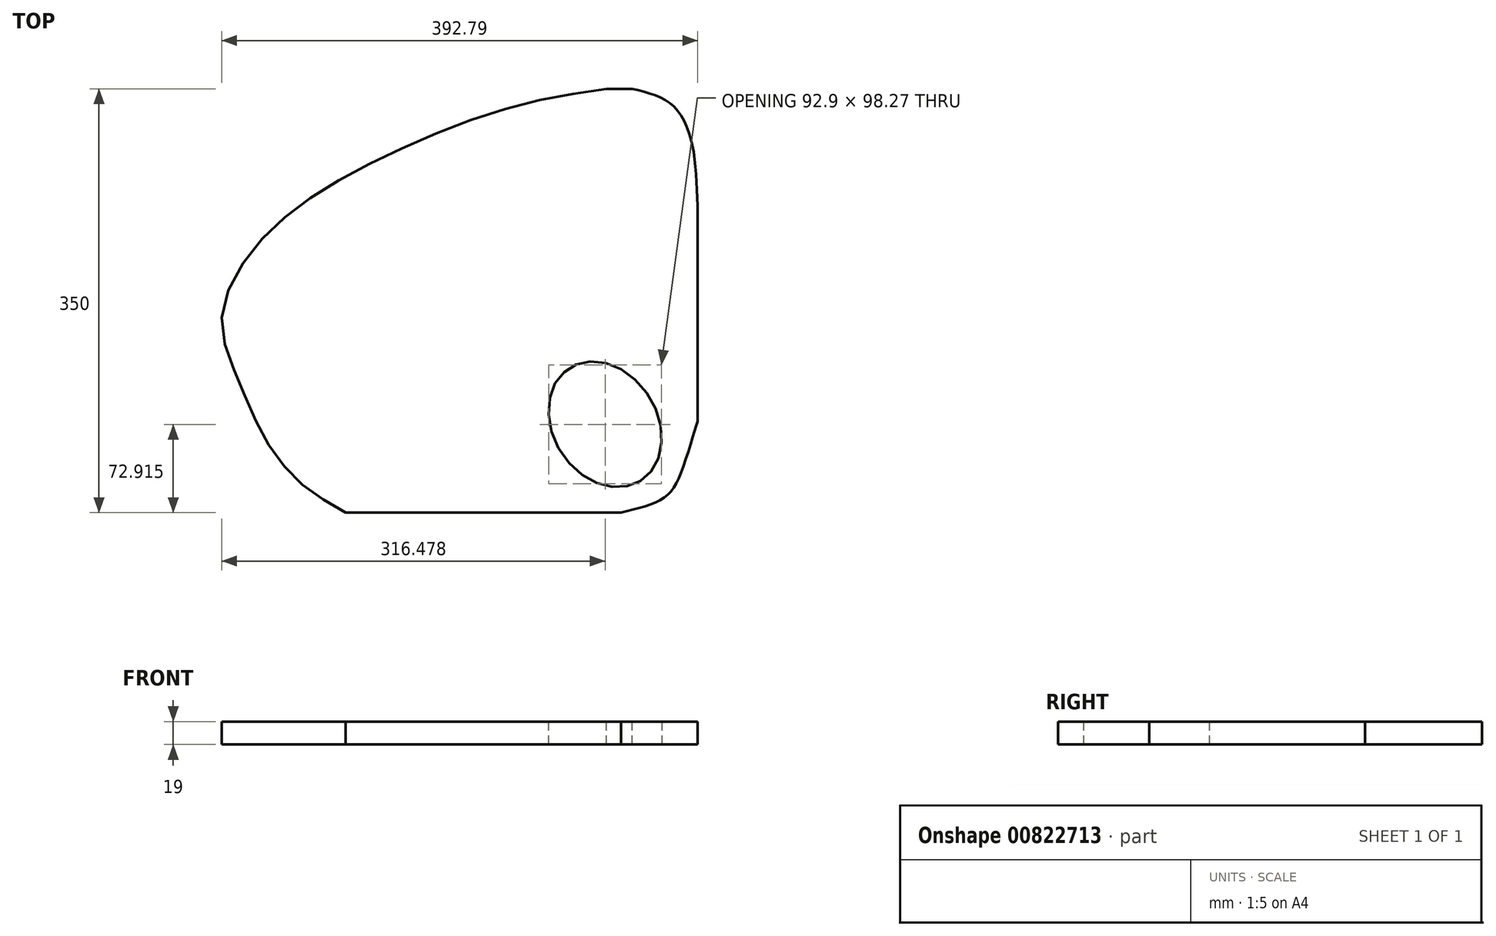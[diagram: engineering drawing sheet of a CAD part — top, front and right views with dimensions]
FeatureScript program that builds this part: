
annotation { "Feature Type Name" : "Feature", "Feature Type Description" : "" }
export const myFeature = defineFeature(function(context is Context, id is Id, definition is map)
    precondition{}
    {
        {
            var Q0;
            Q0=qCreatedBy(makeId("Top.planeOp"),FACE);
            var sketch = newSketch(context, id + "F0", { "sketchPlane" : qUnion([Q0])});
            skLineSegment(sketch, "E0.bottom", {"start": v(200, -175) * mm, "end": v(-200, -175) * mm});
            skLineSegment(sketch, "E0.top", {"start": v(200, 175) * mm, "end": v(-200, 175) * mm});
            skLineSegment(sketch, "E0.left", {"start": v(200, -175) * mm, "end": v(200, 175) * mm});
            skLineSegment(sketch, "E0.right", {"start": v(-200, -175) * mm, "end": v(-200, 175) * mm});
            skPoint(sketch, "E0.middle", {"position": v(0, 0) * mm});
            skSolve(sketch);
        }
        {
            var Q0;
            Q0 = qSketchRegion(id + "F0", true);
            extrude(context, id + "F1", {"entities" : qUnion([Q0]), "depth" : 19 * mm, "offsetDistance" : 25 * mm});
        }
        {
            var Q0;
            Q0=makeQuery(id+"F1.opExtrude","CAP_FACE",FACE,{"disambiguationData":[OSD([sQuery(id+"F0.wireOp",EDGE,"E0.bottom"),sQuery(id+"F0.wireOp",EDGE,"E0.top"),sQuery(id+"F0.wireOp",EDGE,"E0.left"),sQuery(id+"F0.wireOp",EDGE,"E0.right")])],"isStart":false});
            var sketch = newSketch(context, id + "F2", { "sketchPlane" : qUnion([Q0])});
            skFitSpline(sketch, "E1", {"points": [v(136.72, -175) * mm, v(172.05, -162.82) * mm, v(188.36, -136.73) * mm, v(200, -99.76) * mm, v(200, -100.3) * mm], "startDerivative": vector(122.12, 28.84) * mm, "endDerivative": vector(-1.98, -21.44) * mm});
            skFitSpline(sketch, "E2", {"points": [v(-90.53, -175) * mm, v(-128.58, -149.77) * mm, v(-157.94, -112.26) * mm, v(-179.68, -63.88) * mm, v(-192.73, -14.95) * mm, v(-168.81, 39.96) * mm, v(-117.7, 86.17) * mm, v(-43.77, 125.85) * mm, v(44.84, 159.56) * mm, v(124.76, 175) * mm], "startDerivative": vector(-425.65, 242.3) * mm, "endDerivative": vector(630.15, 93.96) * mm});
            skFitSpline(sketch, "E3", {"points": [v(145.96, 175) * mm, v(176.95, 163.36) * mm, v(194.34, 134) * mm, v(200, 78.56) * mm], "startDerivative": vector(112.28, -26.16) * mm, "endDerivative": vector(5.31, -150.88) * mm});
            skEllipse(sketch, "E4", {"center": v(123.69, -102.08) * mm, "majorRadius": 55.01 * mm, "minorRadius": 43.08 * mm, "majorAxis": v(0.53, -0.85)});
            skSolve(sketch);
        }
        {
            var Q0;
            Q0 = qSketchRegion(id + "F2", true);
            var Q1;
            {var subQ0=sQuery(id+"F2.wireOp",EDGE,"E2");Q1=makeQuery(id+"F2.imprint","IMPRINT",FACE,{"disambiguationData":[TD([[makeQuery(id+"F2.imprint","IMPRINT",EDGE,{"derivedFrom":subQ0}),1.0]])]});}
            extrude(context, id + "F3", {"entities" : qUnion([Q0, Q1]), "operationType" : NewBodyOperationType.REMOVE, "endBound" : BoundingType.THROUGH_ALL, "oppositeDirection" : true, "depth" : 25 * mm, "offsetDistance" : 25 * mm});
        }
        {
            var Q0;
            {var subQ0=sQuery(id+"F2.wireOp",EDGE,"E3");Q0=makeQuery(id+"F2.imprint","IMPRINT",FACE,{"disambiguationData":[TD([[makeQuery(id+"F2.imprint","IMPRINT",EDGE,{"derivedFrom":subQ0}),1.0]])]});}
            extrude(context, id + "F4", {"entities" : qUnion([Q0]), "operationType" : NewBodyOperationType.REMOVE, "endBound" : BoundingType.THROUGH_ALL, "oppositeDirection" : true, "depth" : 25 * mm, "offsetDistance" : 25 * mm});
        }
        {
            var Q0;
            {var subQ0=sQuery(id+"F2.wireOp",EDGE,"E1");var subQ1=makeQuery(id+"F1.opExtrude","CAP_EDGE",EDGE,{"disambiguationData":[OSD([sQuery(id+"F0.wireOp",EDGE,"E0.bottom")])],"isStart":false});var subQ2=makeQuery(id+"F2.imprint","INTERSECT",VERTEX,{"derivedFrom":[subQ1,subQ0]});Q0=makeQuery(id+"F2.imprint","IMPRINT",FACE,{"disambiguationData":[TD([[makeQuery(id+"F2.imprint","IMPRINT",EDGE,{"disambiguationData":[TD([[subQ2,-1.0]])],"derivedFrom":subQ0}),-1.0]])]});}
            extrude(context, id + "F5", {"entities" : qUnion([Q0]), "operationType" : NewBodyOperationType.REMOVE, "endBound" : BoundingType.THROUGH_ALL, "oppositeDirection" : true, "depth" : 25 * mm, "offsetDistance" : 25 * mm});
        }
        {
            var Q0;
            Q0 = qSketchRegion(id + "F2", true);
            extrude(context, id + "F6", {"entities" : qUnion([Q0]), "operationType" : NewBodyOperationType.REMOVE, "endBound" : BoundingType.THROUGH_ALL, "oppositeDirection" : true, "depth" : 25 * mm, "offsetDistance" : 25 * mm});
        }
    });
